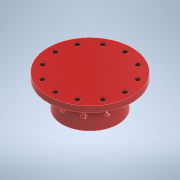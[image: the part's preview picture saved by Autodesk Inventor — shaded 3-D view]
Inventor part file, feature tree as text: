
AUTODESK INVENTOR PART (.ipt)
format: ipt  version: 2022.2 (Build 262287000, 287)  size: 234,496 bytes
history: native  units: mm
features: sketch x4, extrude x2, hole x2, plane x1, pattern_circular x1
ambient origin geometry x8: Origin, YZ Plane, XZ Plane, XY Plane, X Axis, Y Axis, Z Axis, Center Point
bodies: Body1 (feature_tree)
feature tree (10):
  extrude  "Extrusion26"  Depth=8.0mm
  hole  "Hole9"  [1 undecoded]
  extrude  "Extrusion29"  Depth=10.0mm
  plane  "Work Plane6"
  hole  "Hole10"  [1 undecoded]
  pattern_circular  "Circular Pattern1"  [2 undecoded]
  sketch  "Sketch51"  dims[d242=114.3mm d243=8.0mm]
  sketch  "Sketch58"  dims[d244=0.0mm d294=47.625mm]
  sketch  "Sketch59"  dims[d295=120.0mm d297=360.0deg]
  sketch  "Sketch60"  dims[d299=5.105mm d300=6.0mm d301=6.3754mm d302=9.525mm d303=14.3117mm d304=8.0mm d305=0.0mm d306=76.2mm d307=9.525mm d308=35.0mm d309=0.0mm d310=6.3754mm d311=6.0mm d312=6.985mm d313=5.76834mm d314=14.3117mm d315=10.0mm d316=0.0mm d317=100.0mm d318=360.0deg d64=1.0mm d65=1.0mm d66=1.0mm d67=0.15mm d68=0.25mm d69=0.375mm d70=14.3117mm d71=0.75mm d72=20.594885mm d73=0.0625mm d74=0.75mm d75=0.375mm]
note: 4 required parameter values undecoded (feature->parameter linkage not recoverable at this tier; creation-order binding heuristic only, values carry confidence <= 0.55)
